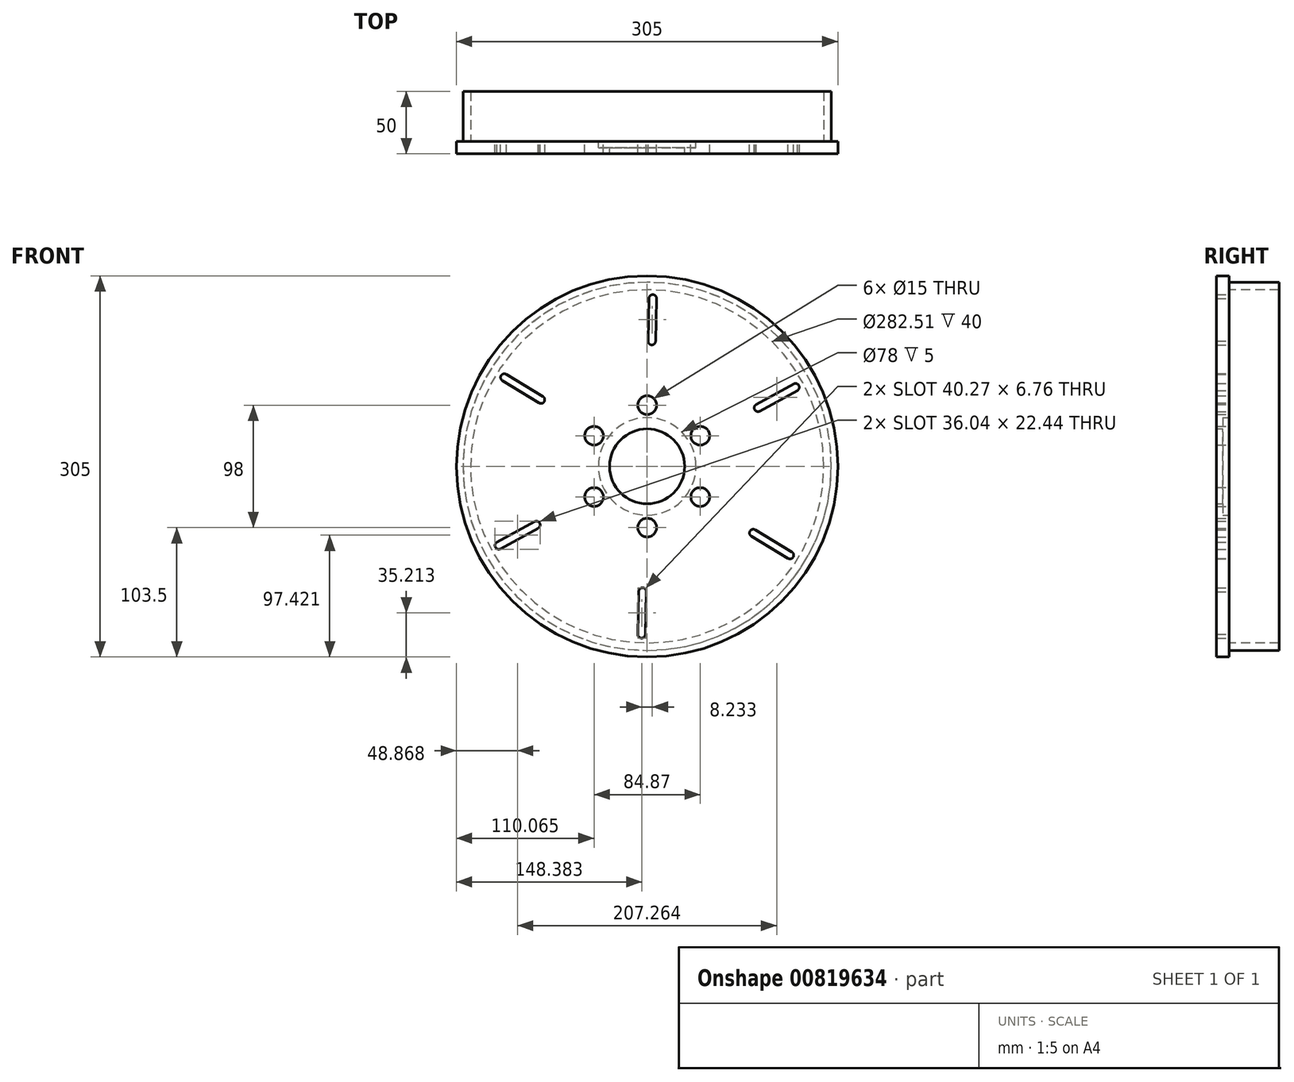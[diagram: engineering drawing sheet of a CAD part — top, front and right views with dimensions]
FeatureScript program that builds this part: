
annotation { "Feature Type Name" : "Feature", "Feature Type Description" : "" }
export const myFeature = defineFeature(function(context is Context, id is Id, definition is map)
    precondition{}
    {
        {
            var Q0;
            Q0=qCreatedBy(makeId("Front.planeOp"),FACE);
            var sketch = newSketch(context, id + "F0", { "sketchPlane" : qUnion([Q0])});
            skCircle(sketch, "E0", {"center": v(0, 0) * mm, "radius": 30 * mm});
            skCircle(sketch, "E1", {"center": v(0, 0) * mm, "radius": 49 * mm, "construction": true});
            skCircle(sketch, "E2", {"center": v(0, 0) * mm, "radius": 152.5 * mm});
            skCircle(sketch, "E3", {"center": v(0, 49) * mm, "radius": 7.5 * mm});
            skCircle(sketch, "E4.1.0", {"center": v(-42.44, 24.5) * mm, "radius": 7.5 * mm});
            skCircle(sketch, "E4.2.0", {"center": v(-42.44, -24.5) * mm, "radius": 7.5 * mm});
            skCircle(sketch, "E5.1.3.0", {"center": v(0, -49) * mm, "radius": 7.5 * mm});
            skCircle(sketch, "E5.1.4.0", {"center": v(42.44, -24.5) * mm, "radius": 7.5 * mm});
            skCircle(sketch, "E5.1.5.0", {"center": v(42.44, 24.5) * mm, "radius": 7.5 * mm});
            skCircle(sketch, "E6", {"center": v(0, 0) * mm, "radius": 134.5 * mm, "construction": true});
            skArc(sketch, "E7", {"start": v(7.5, 134.3) * mm, "mid": v(4.6, 137.42) * mm, "end": v(1.5, 134.5) * mm});
            skLineSegment(sketch, "E8", {"start": v(0, 0) * mm, "end": v(3.62, 97.15) * mm, "construction": true});
            skArc(sketch, "E9", {"start": v(0.74, 100.28) * mm, "mid": v(3.63, 97.15) * mm, "end": v(6.73, 100.08) * mm});
            skLineSegment(sketch, "E10", {"start": v(7.5, 134.3) * mm, "end": v(6.73, 100.08) * mm});
            skLineSegment(sketch, "E11", {"start": v(0.73, 100.15) * mm, "end": v(1.5, 134.5) * mm});
            skArc(sketch, "E12.1.0", {"start": v(-112.55, 73.64) * mm, "mid": v(-116.71, 72.7) * mm, "end": v(-115.72, 68.54) * mm});
            skLineSegment(sketch, "E12.1.1", {"start": v(-112.55, 73.64) * mm, "end": v(-83.3, 55.87) * mm});
            skArc(sketch, "E12.1.2", {"start": v(-86.48, 50.78) * mm, "mid": v(-82.32, 51.72) * mm, "end": v(-83.3, 55.87) * mm});
            skLineSegment(sketch, "E12.1.3", {"start": v(-86.37, 50.71) * mm, "end": v(-115.72, 68.54) * mm});
            skArc(sketch, "E12.2.0", {"start": v(-120.05, -60.65) * mm, "mid": v(-121.31, -64.73) * mm, "end": v(-117.22, -65.95) * mm});
            skLineSegment(sketch, "E12.2.1", {"start": v(-120.05, -60.65) * mm, "end": v(-90.04, -44.21) * mm});
            skArc(sketch, "E12.2.2", {"start": v(-87.22, -49.5) * mm, "mid": v(-85.95, -45.43) * mm, "end": v(-90.04, -44.21) * mm});
            skLineSegment(sketch, "E12.2.3", {"start": v(-87.1, -49.44) * mm, "end": v(-117.22, -65.95) * mm});
            skArc(sketch, "E13.3.3.0", {"start": v(-7.5, -134.3) * mm, "mid": v(-4.6, -137.42) * mm, "end": v(-1.5, -134.5) * mm});
            skLineSegment(sketch, "E13.4.3.0", {"start": v(-7.5, -134.3) * mm, "end": v(-6.73, -100.08) * mm});
            skArc(sketch, "E13.7.3.0", {"start": v(-0.74, -100.28) * mm, "mid": v(-3.63, -97.15) * mm, "end": v(-6.73, -100.08) * mm});
            skLineSegment(sketch, "E13.11.3.0", {"start": v(-0.73, -100.15) * mm, "end": v(-1.5, -134.5) * mm});
            skArc(sketch, "E13.3.4.0", {"start": v(112.55, -73.64) * mm, "mid": v(116.71, -72.7) * mm, "end": v(115.72, -68.54) * mm});
            skLineSegment(sketch, "E13.4.4.0", {"start": v(112.55, -73.64) * mm, "end": v(83.3, -55.87) * mm});
            skArc(sketch, "E13.7.4.0", {"start": v(86.48, -50.78) * mm, "mid": v(82.32, -51.72) * mm, "end": v(83.3, -55.87) * mm});
            skLineSegment(sketch, "E13.11.4.0", {"start": v(86.37, -50.71) * mm, "end": v(115.72, -68.54) * mm});
            skArc(sketch, "E13.3.5.0", {"start": v(120.05, 60.65) * mm, "mid": v(121.31, 64.73) * mm, "end": v(117.22, 65.95) * mm});
            skLineSegment(sketch, "E13.4.5.0", {"start": v(120.05, 60.65) * mm, "end": v(90.04, 44.21) * mm});
            skArc(sketch, "E13.7.5.0", {"start": v(87.22, 49.5) * mm, "mid": v(85.95, 45.43) * mm, "end": v(90.04, 44.21) * mm});
            skLineSegment(sketch, "E13.11.5.0", {"start": v(87.1, 49.44) * mm, "end": v(117.22, 65.95) * mm});
            skSolve(sketch);
        }
        {
            var Q0;
            Q0=makeQuery(id+"F0.imprint","IMPRINT",FACE,{"disambiguationData":[TD([[makeQuery(id+"F0.imprint","IMPRINT",EDGE,{"derivedFrom":sQuery(id+"F0.wireOp",EDGE,"E0")}),-1.0]])]});
            extrude(context, id + "F1", {"entities" : qUnion([Q0]), "depth" : 10 * mm, "offsetDistance" : 25 * mm});
        }
        {
            var Q0;
            Q0=makeQuery(id+"F1.opExtrude","CAP_FACE",FACE,{"disambiguationData":[OSD([sQuery(id+"F0.wireOp",EDGE,"E0"),sQuery(id+"F0.wireOp",EDGE,"E2"),sQuery(id+"F0.wireOp",EDGE,"E3"),sQuery(id+"F0.wireOp",EDGE,"E4.1.0"),sQuery(id+"F0.wireOp",EDGE,"E4.2.0"),sQuery(id+"F0.wireOp",EDGE,"E5.1.3.0"),sQuery(id+"F0.wireOp",EDGE,"E5.1.4.0"),sQuery(id+"F0.wireOp",EDGE,"E5.1.5.0"),sQuery(id+"F0.wireOp",EDGE,"E7"),sQuery(id+"F0.wireOp",EDGE,"E9"),sQuery(id+"F0.wireOp",EDGE,"E10"),sQuery(id+"F0.wireOp",EDGE,"E11"),sQuery(id+"F0.wireOp",EDGE,"E12.1.0"),sQuery(id+"F0.wireOp",EDGE,"E12.1.1"),sQuery(id+"F0.wireOp",EDGE,"E12.1.2"),sQuery(id+"F0.wireOp",EDGE,"E12.1.3"),sQuery(id+"F0.wireOp",EDGE,"E12.2.0"),sQuery(id+"F0.wireOp",EDGE,"E12.2.1"),sQuery(id+"F0.wireOp",EDGE,"E12.2.2"),sQuery(id+"F0.wireOp",EDGE,"E12.2.3"),sQuery(id+"F0.wireOp",EDGE,"E13.3.3.0"),sQuery(id+"F0.wireOp",EDGE,"E13.4.3.0"),sQuery(id+"F0.wireOp",EDGE,"E13.7.3.0"),sQuery(id+"F0.wireOp",EDGE,"E13.11.3.0"),sQuery(id+"F0.wireOp",EDGE,"E13.3.4.0"),sQuery(id+"F0.wireOp",EDGE,"E13.4.4.0"),sQuery(id+"F0.wireOp",EDGE,"E13.7.4.0"),sQuery(id+"F0.wireOp",EDGE,"E13.11.4.0"),sQuery(id+"F0.wireOp",EDGE,"E13.3.5.0"),sQuery(id+"F0.wireOp",EDGE,"E13.4.5.0"),sQuery(id+"F0.wireOp",EDGE,"E13.7.5.0"),sQuery(id+"F0.wireOp",EDGE,"E13.11.5.0")])],"isStart":true});
            var sketch = newSketch(context, id + "F2", { "sketchPlane" : qUnion([Q0])});
            skCircle(sketch, "E14", {"center": v(0, 0) * mm, "radius": 141.25 * mm});
            skCircle(sketch, "E15", {"center": v(0, 0) * mm, "radius": 147.27 * mm});
            skSolve(sketch);
        }
        {
            var Q0;
            Q0=makeQuery(id+"F2.imprint","IMPRINT",FACE,{"disambiguationData":[TD([[makeQuery(id+"F2.imprint","IMPRINT",EDGE,{"derivedFrom":sQuery(id+"F2.wireOp",EDGE,"E14")}),-1.0]])]});
            extrude(context, id + "F3", {"entities" : qUnion([Q0]), "operationType" : NewBodyOperationType.ADD, "depth" : 40 * mm, "offsetDistance" : 25 * mm});
        }
        {
            var Q0;
            {var subQ0=sQuery(id+"F0.wireOp",EDGE,"E13.7.3.0");var subQ1=sQuery(id+"F0.wireOp",EDGE,"E13.3.3.0");var subQ2=sQuery(id+"F0.wireOp",EDGE,"E12.2.3");var subQ3=sQuery(id+"F0.wireOp",EDGE,"E12.2.2");var subQ4=sQuery(id+"F0.wireOp",EDGE,"E12.2.1");var subQ5=sQuery(id+"F0.wireOp",EDGE,"E12.2.0");var subQ6=sQuery(id+"F0.wireOp",EDGE,"E12.1.3");var subQ7=sQuery(id+"F0.wireOp",EDGE,"E12.1.2");var subQ8=sQuery(id+"F0.wireOp",EDGE,"E12.1.1");var subQ9=sQuery(id+"F0.wireOp",EDGE,"E12.1.0");var subQ10=sQuery(id+"F0.wireOp",EDGE,"E11");var subQ11=sQuery(id+"F0.wireOp",EDGE,"E4.2.0");var subQ12=sQuery(id+"F0.wireOp",EDGE,"E3");var subQ13=sQuery(id+"F0.wireOp",EDGE,"E4.1.0");var subQ14=sQuery(id+"F0.wireOp",EDGE,"E13.4.3.0");var subQ15=sQuery(id+"F0.wireOp",EDGE,"E0");var subQ16=sQuery(id+"F0.wireOp",EDGE,"E9");var subQ17=sQuery(id+"F0.wireOp",EDGE,"E5.1.3.0");var subQ18=sQuery(id+"F0.wireOp",EDGE,"E5.1.4.0");var subQ19=sQuery(id+"F0.wireOp",EDGE,"E5.1.5.0");var subQ20=sQuery(id+"F0.wireOp",EDGE,"E7");var subQ21=sQuery(id+"F0.wireOp",EDGE,"E10");var subQ22=sQuery(id+"F0.wireOp",EDGE,"E13.11.3.0");var subQ23=sQuery(id+"F0.wireOp",EDGE,"E13.3.4.0");var subQ24=sQuery(id+"F0.wireOp",EDGE,"E13.4.4.0");var subQ25=sQuery(id+"F0.wireOp",EDGE,"E13.7.4.0");var subQ26=sQuery(id+"F0.wireOp",EDGE,"E13.11.4.0");var subQ27=sQuery(id+"F0.wireOp",EDGE,"E13.3.5.0");var subQ28=sQuery(id+"F0.wireOp",EDGE,"E13.4.5.0");var subQ29=sQuery(id+"F0.wireOp",EDGE,"E13.7.5.0");var subQ30=sQuery(id+"F0.wireOp",EDGE,"E13.11.5.0");Q0=makeQuery(id+"F3.boolean.opBoolean","SPLIT",FACE,{"disambiguationData":[TD([makeQuery(id+"F1.opExtrude","SWEPT_FACE",FACE,{"disambiguationData":[OSD([subQ15])]})])],"derivedFrom":makeQuery(id+"F1.opExtrude","CAP_FACE",FACE,{"disambiguationData":[OSD([subQ15,sQuery(id+"F0.wireOp",EDGE,"E2"),subQ12,subQ13,subQ11,subQ17,subQ18,subQ19,subQ20,subQ16,subQ21,subQ10,subQ9,subQ8,subQ7,subQ6,subQ5,subQ4,subQ3,subQ2,subQ1,subQ14,subQ0,subQ22,subQ23,subQ24,subQ25,subQ26,subQ27,subQ28,subQ29,subQ30])],"isStart":true})});}
            var sketch = newSketch(context, id + "F4", { "sketchPlane" : qUnion([Q0])});
            skCircle(sketch, "E16", {"center": v(0, 0) * mm, "radius": 39 * mm});
            skSolve(sketch);
        }
        {
            var Q0;
            Q0=makeQuery(id+"F4.imprint","IMPRINT",FACE,{"disambiguationData":[TD([[makeQuery(id+"F4.imprint","IMPRINT",EDGE,{"derivedFrom":sQuery(id+"F4.wireOp",EDGE,"E16")}),1.0]])]});
            extrude(context, id + "F5", {"entities" : qUnion([Q0]), "operationType" : NewBodyOperationType.REMOVE, "oppositeDirection" : true, "depth" : 5 * mm, "offsetDistance" : 25 * mm});
        }
    });
